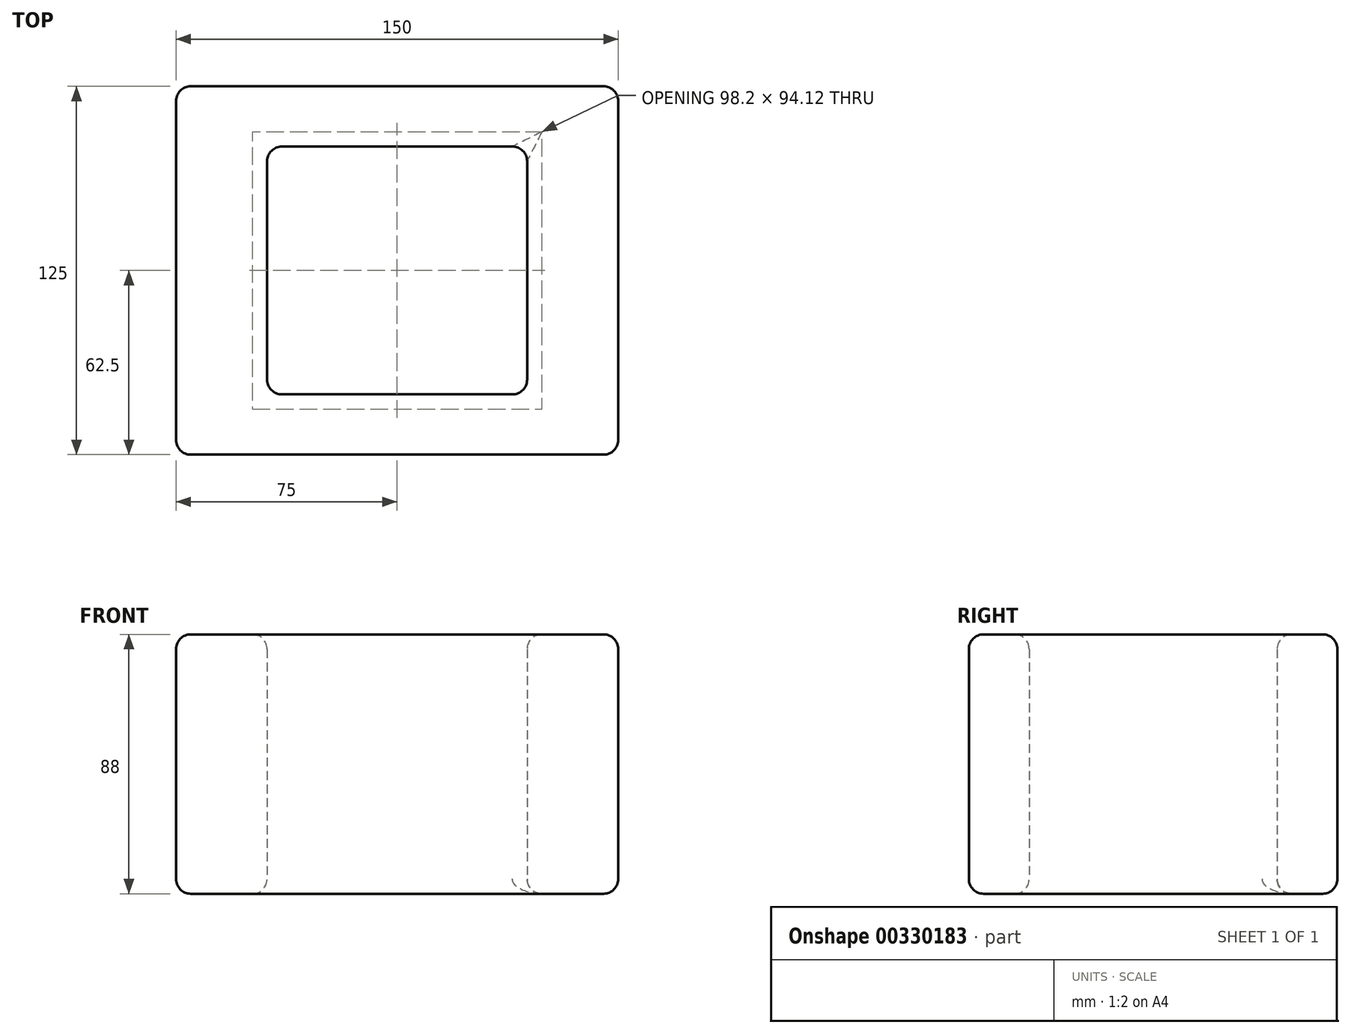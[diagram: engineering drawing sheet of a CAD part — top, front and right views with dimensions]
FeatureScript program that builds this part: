
annotation { "Feature Type Name" : "Feature", "Feature Type Description" : "" }
export const myFeature = defineFeature(function(context is Context, id is Id, definition is map)
    precondition{}
    {
        {
            var Q0;
            Q0=qCreatedBy(makeId("Top.planeOp"),FACE);
            var sketch = newSketch(context, id + "F0", { "sketchPlane" : qUnion([Q0])});
            skLineSegment(sketch, "E0.bottom", {"start": v(75, -62.5) * mm, "end": v(-75, -62.5) * mm});
            skLineSegment(sketch, "E0.top", {"start": v(75, 62.5) * mm, "end": v(-75, 62.5) * mm});
            skLineSegment(sketch, "E0.left", {"start": v(75, -62.5) * mm, "end": v(75, 62.5) * mm});
            skLineSegment(sketch, "E0.right", {"start": v(-75, -62.5) * mm, "end": v(-75, 62.5) * mm});
            skPoint(sketch, "E0.middle", {"position": v(0, 0) * mm});
            skLineSegment(sketch, "E1.bottom", {"start": v(-44.1, 42.06) * mm, "end": v(44.1, 42.06) * mm});
            skLineSegment(sketch, "E1.top", {"start": v(-44.1, -42.06) * mm, "end": v(44.1, -42.06) * mm});
            skLineSegment(sketch, "E1.left", {"start": v(-44.1, 42.06) * mm, "end": v(-44.1, -42.06) * mm});
            skLineSegment(sketch, "E1.right", {"start": v(44.1, 42.06) * mm, "end": v(44.1, -42.06) * mm});
            skSolve(sketch);
        }
        {
            var Q0;
            Q0 = qSketchRegion(id + "F0", true);
            extrude(context, id + "F1", {"entities" : qUnion([Q0]), "depth" : 88 * mm});
        }
        {
            var Q0;
            Q0=makeQuery(id+"F1.opExtrude","CAP_EDGE",EDGE,{"disambiguationData":[OSD([sQuery(id+"F0.wireOp",EDGE,"E0.right")])],"isStart":false});
            var Q1;
            Q1=makeQuery(id+"F1.opExtrude","SWEPT_FACE",FACE,{"disambiguationData":[OSD([sQuery(id+"F0.wireOp",EDGE,"E0.right")])]});
            fillet(context, id + "F2", {"entities" : qUnion([Q0, Q1]), "radius" : 5 * mm, "tangentPropagation" : true, "allowEdgeOverflow" : false});
        }
        {
            var Q0;
            Q0=makeQuery(id+"F1.opExtrude","SWEPT_FACE",FACE,{"disambiguationData":[OSD([sQuery(id+"F0.wireOp",EDGE,"E0.bottom")])]});
            fillet(context, id + "F3", {"entities" : qUnion([Q0]), "radius" : 5 * mm, "tangentPropagation" : true, "allowEdgeOverflow" : false});
        }
        {
            var Q0;
            Q0=makeQuery(id+"F1.opExtrude","SWEPT_FACE",FACE,{"disambiguationData":[OSD([sQuery(id+"F0.wireOp",EDGE,"E0.right")])]});
            var Q1;
            {var subQ0=sQuery(id+"F0.wireOp",EDGE,"E0.right");Q1=makeQuery(id+"F2.opFillet","BLEND_FACE",FACE,{"disambiguationData":[OSD([subQ0]),TDD([makeQuery(id+"F1.opExtrude","CAP_EDGE",EDGE,{"disambiguationData":[OSD([subQ0])],"isStart":true})])]});}
            var Q2;
            {var subQ0=sQuery(id+"F0.wireOp",EDGE,"E0.right");Q2=makeQuery(id+"F2.opFillet","BLEND_EDGE",EDGE,{"blendedFrom":[makeQuery(id+"F1.opExtrude","CAP_EDGE",EDGE,{"disambiguationData":[OSD([subQ0])],"isStart":true}),makeQuery(id+"F1.opExtrude","SWEPT_FACE",FACE,{"disambiguationData":[OSD([subQ0])]})],"blendedInto":[makeQuery(id+"F1.opExtrude","SWEPT_FACE",FACE,{"disambiguationData":[OSD([subQ0])]})]});}
            var Q3;
            Q3=makeQuery(id+"F2.opFillet","BLEND_FACE",FACE,{"disambiguationData":[OSD([sQuery(id+"F0.wireOp",EDGE,"E0.bottom"),sQuery(id+"F0.wireOp",EDGE,"E0.right")])]});
            var Q4;
            Q4=makeQuery(id+"F1.opExtrude","CAP_FACE",FACE,{"disambiguationData":[OSD([sQuery(id+"F0.wireOp",EDGE,"E0.bottom"),sQuery(id+"F0.wireOp",EDGE,"E0.top"),sQuery(id+"F0.wireOp",EDGE,"E0.left"),sQuery(id+"F0.wireOp",EDGE,"E0.right"),sQuery(id+"F0.wireOp",EDGE,"E1.bottom"),sQuery(id+"F0.wireOp",EDGE,"E1.top"),sQuery(id+"F0.wireOp",EDGE,"E1.left"),sQuery(id+"F0.wireOp",EDGE,"E1.right")])],"isStart":true});
            var Q5;
            Q5=makeQuery(id+"F1.opExtrude","SWEPT_FACE",FACE,{"disambiguationData":[OSD([sQuery(id+"F0.wireOp",EDGE,"E1.top")])]});
            var Q6;
            {var subQ0=sQuery(id+"F0.wireOp",EDGE,"E0.right");Q6=makeQuery(id+"F2.opFillet","BLEND_EDGE",EDGE,{"blendedFrom":[makeQuery(id+"F1.opExtrude","SWEPT_EDGE",EDGE,{"disambiguationData":[OSD([sQuery(id+"F0.wireOp",EDGE,"E0.bottom"),subQ0])]}),makeQuery(id+"F1.opExtrude","SWEPT_FACE",FACE,{"disambiguationData":[OSD([subQ0])]})],"blendedInto":[makeQuery(id+"F1.opExtrude","SWEPT_FACE",FACE,{"disambiguationData":[OSD([subQ0])]})]});}
            var Q7;
            Q7=makeQuery(id+"F1.opExtrude","SWEPT_FACE",FACE,{"disambiguationData":[OSD([sQuery(id+"F0.wireOp",EDGE,"E1.left")])]});
            var Q8;
            Q8=makeQuery(id+"F1.opExtrude","SWEPT_EDGE",EDGE,{"disambiguationData":[OSD([sQuery(id+"F0.wireOp",EDGE,"E1.top"),sQuery(id+"F0.wireOp",EDGE,"E1.left")])]});
            var Q9;
            {var subQ0=sQuery(id+"F0.wireOp",EDGE,"E0.right");Q9=makeQuery(id+"F2.opFillet","BLEND_EDGE",EDGE,{"blendedFrom":[makeQuery(id+"F1.opExtrude","CAP_EDGE",EDGE,{"disambiguationData":[OSD([subQ0])],"isStart":true}),makeQuery(id+"F1.opExtrude","CAP_FACE",FACE,{"disambiguationData":[OSD([sQuery(id+"F0.wireOp",EDGE,"E0.bottom"),sQuery(id+"F0.wireOp",EDGE,"E0.top"),sQuery(id+"F0.wireOp",EDGE,"E0.left"),subQ0,sQuery(id+"F0.wireOp",EDGE,"E1.bottom"),sQuery(id+"F0.wireOp",EDGE,"E1.top"),sQuery(id+"F0.wireOp",EDGE,"E1.left"),sQuery(id+"F0.wireOp",EDGE,"E1.right")])],"isStart":true})],"blendedInto":[makeQuery(id+"F1.opExtrude","CAP_FACE",FACE,{"disambiguationData":[OSD([sQuery(id+"F0.wireOp",EDGE,"E0.bottom"),sQuery(id+"F0.wireOp",EDGE,"E0.top"),sQuery(id+"F0.wireOp",EDGE,"E0.left"),subQ0,sQuery(id+"F0.wireOp",EDGE,"E1.bottom"),sQuery(id+"F0.wireOp",EDGE,"E1.top"),sQuery(id+"F0.wireOp",EDGE,"E1.left"),sQuery(id+"F0.wireOp",EDGE,"E1.right")])],"isStart":true})]});}
            var Q10;
            {var subQ0=sQuery(id+"F0.wireOp",EDGE,"E0.bottom");Q10=makeQuery(id+"F2.opFillet","BLEND_EDGE",EDGE,{"blendedFrom":[makeQuery(id+"F1.opExtrude","SWEPT_EDGE",EDGE,{"disambiguationData":[OSD([subQ0,sQuery(id+"F0.wireOp",EDGE,"E0.right")])]}),makeQuery(id+"F1.opExtrude","SWEPT_FACE",FACE,{"disambiguationData":[OSD([subQ0])]})],"blendedInto":[makeQuery(id+"F1.opExtrude","SWEPT_FACE",FACE,{"disambiguationData":[OSD([subQ0])]})]});}
            var Q11;
            Q11=makeQuery(id+"F1.opExtrude","CAP_EDGE",EDGE,{"disambiguationData":[OSD([sQuery(id+"F0.wireOp",EDGE,"E1.left")])],"isStart":true});
            var Q12;
            Q12=makeQuery(id+"F1.opExtrude","SWEPT_FACE",FACE,{"disambiguationData":[OSD([sQuery(id+"F0.wireOp",EDGE,"E0.bottom")])]});
            fillet(context, id + "F4", {"entities" : qUnion([Q0, Q1, Q2, Q3, Q4, Q5, Q6, Q7, Q8, Q9, Q10, Q11, Q12]), "radius" : 5 * mm, "tangentPropagation" : true, "allowEdgeOverflow" : false});
        }
        {
            var Q0;
            {var subQ0=sQuery(id+"F0.wireOp",EDGE,"E0.bottom");Q0=makeQuery(id+"F3.opFillet","BLEND_FACE",FACE,{"disambiguationData":[OSD([subQ0]),TDD([makeQuery(id+"F1.opExtrude","CAP_EDGE",EDGE,{"disambiguationData":[OSD([subQ0])],"isStart":true})])]});}
            var Q1;
            {var subQ0=sQuery(id+"F0.wireOp",EDGE,"E0.right");Q1=makeQuery(id+"F2.opFillet","BLEND_FACE",FACE,{"disambiguationData":[OSD([subQ0]),TDD([makeQuery(id+"F1.opExtrude","CAP_EDGE",EDGE,{"disambiguationData":[OSD([subQ0])],"isStart":true})])]});}
            var Q2;
            {var subQ0=sQuery(id+"F0.wireOp",EDGE,"E0.right");var subQ1=sQuery(id+"F0.wireOp",EDGE,"E0.bottom");Q2=makeQuery(id+"F4.opFillet","BLEND_FACE",FACE,{"disambiguationData":[OSD([subQ1,subQ0]),TDD([makeQuery(id+"F3.opFillet","BLEND_EDGE",EDGE,{"blendedFrom":[makeQuery(id+"F1.opExtrude","CAP_EDGE",EDGE,{"disambiguationData":[OSD([subQ1])],"isStart":true}),makeQuery(id+"F2.opFillet","BLEND_FACE",FACE,{"disambiguationData":[OSD([subQ0]),TDD([makeQuery(id+"F1.opExtrude","CAP_EDGE",EDGE,{"disambiguationData":[OSD([subQ0])],"isStart":true})])]})],"blendedInto":[makeQuery(id+"F2.opFillet","BLEND_FACE",FACE,{"disambiguationData":[OSD([subQ0]),TDD([makeQuery(id+"F1.opExtrude","CAP_EDGE",EDGE,{"disambiguationData":[OSD([subQ0])],"isStart":true})])]})]})])]});}
            var Q3;
            Q3=makeQuery(id+"F1.opExtrude","CAP_FACE",FACE,{"disambiguationData":[OSD([sQuery(id+"F0.wireOp",EDGE,"E0.bottom"),sQuery(id+"F0.wireOp",EDGE,"E0.top"),sQuery(id+"F0.wireOp",EDGE,"E0.left"),sQuery(id+"F0.wireOp",EDGE,"E0.right"),sQuery(id+"F0.wireOp",EDGE,"E1.bottom"),sQuery(id+"F0.wireOp",EDGE,"E1.top"),sQuery(id+"F0.wireOp",EDGE,"E1.left"),sQuery(id+"F0.wireOp",EDGE,"E1.right")])],"isStart":true});
            var Q4;
            Q4=makeQuery(id+"F1.opExtrude","SWEPT_FACE",FACE,{"disambiguationData":[OSD([sQuery(id+"F0.wireOp",EDGE,"E0.bottom")])]});
            var Q5;
            {var subQ0=sQuery(id+"F0.wireOp",EDGE,"E0.right");var subQ1=makeQuery(id+"F1.opExtrude","CAP_EDGE",EDGE,{"disambiguationData":[OSD([subQ0])],"isStart":true});Q5=makeQuery(id+"F4.opFillet","BLEND_EDGE",EDGE,{"blendedFrom":[makeQuery(id+"F2.opFillet","BLEND_EDGE",EDGE,{"blendedFrom":[makeQuery(id+"F1.opExtrude","SWEPT_EDGE",EDGE,{"disambiguationData":[OSD([sQuery(id+"F0.wireOp",EDGE,"E0.bottom"),subQ0])]}),subQ1],"blendedInto":[]}),makeQuery(id+"F2.opFillet","BLEND_FACE",FACE,{"disambiguationData":[OSD([subQ0]),TDD([subQ1])]})],"blendedInto":[makeQuery(id+"F2.opFillet","BLEND_FACE",FACE,{"disambiguationData":[OSD([subQ0]),TDD([subQ1])]})]});}
            var Q6;
            {var subQ0=sQuery(id+"F0.wireOp",EDGE,"E0.bottom");var subQ1=makeQuery(id+"F1.opExtrude","CAP_EDGE",EDGE,{"disambiguationData":[OSD([subQ0])],"isStart":true});var subQ2=sQuery(id+"F0.wireOp",EDGE,"E0.right");Q6=makeQuery(id+"F4.opFillet","BLEND_EDGE",EDGE,{"blendedFrom":[makeQuery(id+"F3.opFillet","BLEND_EDGE",EDGE,{"blendedFrom":[subQ1,makeQuery(id+"F2.opFillet","BLEND_FACE",FACE,{"disambiguationData":[OSD([subQ2]),TDD([makeQuery(id+"F1.opExtrude","CAP_EDGE",EDGE,{"disambiguationData":[OSD([subQ2])],"isStart":true})])]})],"blendedInto":[makeQuery(id+"F2.opFillet","BLEND_FACE",FACE,{"disambiguationData":[OSD([subQ2]),TDD([makeQuery(id+"F1.opExtrude","CAP_EDGE",EDGE,{"disambiguationData":[OSD([subQ2])],"isStart":true})])]})]}),makeQuery(id+"F3.opFillet","BLEND_FACE",FACE,{"disambiguationData":[OSD([subQ0]),TDD([subQ1])]})],"blendedInto":[makeQuery(id+"F3.opFillet","BLEND_FACE",FACE,{"disambiguationData":[OSD([subQ0]),TDD([subQ1])]})]});}
            var Q7;
            {var subQ0=sQuery(id+"F0.wireOp",EDGE,"E0.bottom");Q7=makeQuery(id+"F3.opFillet","BLEND_EDGE",EDGE,{"blendedFrom":[makeQuery(id+"F1.opExtrude","CAP_EDGE",EDGE,{"disambiguationData":[OSD([subQ0])],"isStart":true}),makeQuery(id+"F1.opExtrude","CAP_FACE",FACE,{"disambiguationData":[OSD([subQ0,sQuery(id+"F0.wireOp",EDGE,"E0.top"),sQuery(id+"F0.wireOp",EDGE,"E0.left"),sQuery(id+"F0.wireOp",EDGE,"E0.right"),sQuery(id+"F0.wireOp",EDGE,"E1.bottom"),sQuery(id+"F0.wireOp",EDGE,"E1.top"),sQuery(id+"F0.wireOp",EDGE,"E1.left"),sQuery(id+"F0.wireOp",EDGE,"E1.right")])],"isStart":true})],"blendedInto":[makeQuery(id+"F1.opExtrude","CAP_FACE",FACE,{"disambiguationData":[OSD([subQ0,sQuery(id+"F0.wireOp",EDGE,"E0.top"),sQuery(id+"F0.wireOp",EDGE,"E0.left"),sQuery(id+"F0.wireOp",EDGE,"E0.right"),sQuery(id+"F0.wireOp",EDGE,"E1.bottom"),sQuery(id+"F0.wireOp",EDGE,"E1.top"),sQuery(id+"F0.wireOp",EDGE,"E1.left"),sQuery(id+"F0.wireOp",EDGE,"E1.right")])],"isStart":true})]});}
            var Q8;
            {var subQ0=sQuery(id+"F0.wireOp",EDGE,"E0.bottom");Q8=makeQuery(id+"F3.opFillet","BLEND_EDGE",EDGE,{"blendedFrom":[makeQuery(id+"F1.opExtrude","CAP_EDGE",EDGE,{"disambiguationData":[OSD([subQ0])],"isStart":true}),makeQuery(id+"F1.opExtrude","SWEPT_FACE",FACE,{"disambiguationData":[OSD([subQ0])]})],"blendedInto":[makeQuery(id+"F1.opExtrude","SWEPT_FACE",FACE,{"disambiguationData":[OSD([subQ0])]})]});}
            var Q9;
            {var subQ0=sQuery(id+"F0.wireOp",EDGE,"E1.left");var subQ1=sQuery(id+"F0.wireOp",EDGE,"E1.top");Q9=makeQuery(id+"F4.opFillet","BLEND_FACE",FACE,{"disambiguationData":[OSD([subQ1,subQ0]),TDD([makeQuery(id+"F1.opExtrude","SWEPT_EDGE",EDGE,{"disambiguationData":[OSD([subQ1,subQ0])]})])]});}
            var Q10;
            Q10=makeQuery(id+"F1.opExtrude","SWEPT_FACE",FACE,{"disambiguationData":[OSD([sQuery(id+"F0.wireOp",EDGE,"E0.right")])]});
            var Q11;
            {var subQ0=sQuery(id+"F0.wireOp",EDGE,"E0.right");Q11=makeQuery(id+"F2.opFillet","BLEND_EDGE",EDGE,{"blendedFrom":[makeQuery(id+"F1.opExtrude","CAP_EDGE",EDGE,{"disambiguationData":[OSD([subQ0])],"isStart":true}),makeQuery(id+"F1.opExtrude","SWEPT_FACE",FACE,{"disambiguationData":[OSD([subQ0])]})],"blendedInto":[makeQuery(id+"F1.opExtrude","SWEPT_FACE",FACE,{"disambiguationData":[OSD([subQ0])]})]});}
            var Q12;
            Q12=makeQuery(id+"F2.opFillet","BLEND_FACE",FACE,{"disambiguationData":[OSD([sQuery(id+"F0.wireOp",EDGE,"E0.bottom"),sQuery(id+"F0.wireOp",EDGE,"E0.right")])]});
            var Q13;
            {var subQ0=sQuery(id+"F0.wireOp",EDGE,"E0.right");Q13=makeQuery(id+"F2.opFillet","BLEND_EDGE",EDGE,{"blendedFrom":[makeQuery(id+"F1.opExtrude","CAP_EDGE",EDGE,{"disambiguationData":[OSD([subQ0])],"isStart":true}),makeQuery(id+"F1.opExtrude","CAP_FACE",FACE,{"disambiguationData":[OSD([sQuery(id+"F0.wireOp",EDGE,"E0.bottom"),sQuery(id+"F0.wireOp",EDGE,"E0.top"),sQuery(id+"F0.wireOp",EDGE,"E0.left"),subQ0,sQuery(id+"F0.wireOp",EDGE,"E1.bottom"),sQuery(id+"F0.wireOp",EDGE,"E1.top"),sQuery(id+"F0.wireOp",EDGE,"E1.left"),sQuery(id+"F0.wireOp",EDGE,"E1.right")])],"isStart":true})],"blendedInto":[makeQuery(id+"F1.opExtrude","CAP_FACE",FACE,{"disambiguationData":[OSD([sQuery(id+"F0.wireOp",EDGE,"E0.bottom"),sQuery(id+"F0.wireOp",EDGE,"E0.top"),sQuery(id+"F0.wireOp",EDGE,"E0.left"),subQ0,sQuery(id+"F0.wireOp",EDGE,"E1.bottom"),sQuery(id+"F0.wireOp",EDGE,"E1.top"),sQuery(id+"F0.wireOp",EDGE,"E1.left"),sQuery(id+"F0.wireOp",EDGE,"E1.right")])],"isStart":true})]});}
            var Q14;
            Q14=makeQuery(id+"F1.opExtrude","SWEPT_FACE",FACE,{"disambiguationData":[OSD([sQuery(id+"F0.wireOp",EDGE,"E1.top")])]});
            var Q15;
            Q15=makeQuery(id+"F1.opExtrude","SWEPT_FACE",FACE,{"disambiguationData":[OSD([sQuery(id+"F0.wireOp",EDGE,"E1.left")])]});
            var Q16;
            {var subQ0=sQuery(id+"F0.wireOp",EDGE,"E1.right");var subQ1=sQuery(id+"F0.wireOp",EDGE,"E1.top");Q16=makeQuery(id+"F4.opFillet","BLEND_FACE",FACE,{"disambiguationData":[OSD([subQ1,subQ0]),TDD([makeQuery(id+"F1.opExtrude","CAP_VERTEX",VERTEX,{"disambiguationData":[OSD([subQ1,subQ0])],"isStart":false})])]});}
            var Q17;
            Q17=makeQuery(id+"F1.opExtrude","CAP_EDGE",EDGE,{"disambiguationData":[OSD([sQuery(id+"F0.wireOp",EDGE,"E0.left")])],"isStart":false});
            var Q18;
            {var subQ0=sQuery(id+"F0.wireOp",EDGE,"E1.bottom");Q18=makeQuery(id+"F4.opFillet","BLEND_FACE",FACE,{"disambiguationData":[OSD([subQ0]),TDD([makeQuery(id+"F1.opExtrude","CAP_EDGE",EDGE,{"disambiguationData":[OSD([subQ0])],"isStart":false})])]});}
            var Q19;
            {var subQ0=sQuery(id+"F0.wireOp",EDGE,"E1.top");Q19=makeQuery(id+"F4.opFillet","BLEND_FACE",FACE,{"disambiguationData":[OSD([subQ0]),TDD([makeQuery(id+"F1.opExtrude","CAP_EDGE",EDGE,{"disambiguationData":[OSD([subQ0])],"isStart":false})])]});}
            var Q20;
            {var subQ0=sQuery(id+"F0.wireOp",EDGE,"E1.right");var subQ1=sQuery(id+"F0.wireOp",EDGE,"E1.top");Q20=makeQuery(id+"F4.opFillet","BLEND_FACE",FACE,{"disambiguationData":[OSD([subQ1,subQ0]),TDD([makeQuery(id+"F1.opExtrude","SWEPT_EDGE",EDGE,{"disambiguationData":[OSD([subQ1,subQ0])]})])]});}
            var Q21;
            {var subQ0=sQuery(id+"F0.wireOp",EDGE,"E0.right");Q21=makeQuery(id+"F2.opFillet","BLEND_EDGE",EDGE,{"blendedFrom":[makeQuery(id+"F1.opExtrude","SWEPT_EDGE",EDGE,{"disambiguationData":[OSD([sQuery(id+"F0.wireOp",EDGE,"E0.bottom"),subQ0])]}),makeQuery(id+"F1.opExtrude","SWEPT_FACE",FACE,{"disambiguationData":[OSD([subQ0])]})],"blendedInto":[makeQuery(id+"F1.opExtrude","SWEPT_FACE",FACE,{"disambiguationData":[OSD([subQ0])]})]});}
            var Q22;
            {var subQ0=sQuery(id+"F0.wireOp",EDGE,"E0.bottom");Q22=makeQuery(id+"F2.opFillet","BLEND_EDGE",EDGE,{"blendedFrom":[makeQuery(id+"F1.opExtrude","SWEPT_EDGE",EDGE,{"disambiguationData":[OSD([subQ0,sQuery(id+"F0.wireOp",EDGE,"E0.right")])]}),makeQuery(id+"F1.opExtrude","SWEPT_FACE",FACE,{"disambiguationData":[OSD([subQ0])]})],"blendedInto":[makeQuery(id+"F1.opExtrude","SWEPT_FACE",FACE,{"disambiguationData":[OSD([subQ0])]})]});}
            var Q23;
            {var subQ0=sQuery(id+"F0.wireOp",EDGE,"E1.right");Q23=makeQuery(id+"F4.opFillet","BLEND_EDGE",EDGE,{"blendedFrom":[makeQuery(id+"F1.opExtrude","CAP_EDGE",EDGE,{"disambiguationData":[OSD([subQ0])],"isStart":false}),makeQuery(id+"F1.opExtrude","SWEPT_FACE",FACE,{"disambiguationData":[OSD([subQ0])]})],"blendedInto":[makeQuery(id+"F1.opExtrude","SWEPT_FACE",FACE,{"disambiguationData":[OSD([subQ0])]})]});}
            var Q24;
            {var subQ0=sQuery(id+"F0.wireOp",EDGE,"E1.right");Q24=makeQuery(id+"F4.opFillet","BLEND_FACE",FACE,{"disambiguationData":[OSD([subQ0]),TDD([makeQuery(id+"F1.opExtrude","CAP_EDGE",EDGE,{"disambiguationData":[OSD([subQ0])],"isStart":false})])]});}
            var Q25;
            Q25=makeQuery(id+"F1.opExtrude","SWEPT_FACE",FACE,{"disambiguationData":[OSD([sQuery(id+"F0.wireOp",EDGE,"E0.left")])]});
            var Q26;
            {var subQ0=sQuery(id+"F0.wireOp",EDGE,"E1.bottom");Q26=makeQuery(id+"F4.opFillet","BLEND_EDGE",EDGE,{"blendedFrom":[makeQuery(id+"F1.opExtrude","CAP_EDGE",EDGE,{"disambiguationData":[OSD([subQ0])],"isStart":false}),makeQuery(id+"F1.opExtrude","SWEPT_FACE",FACE,{"disambiguationData":[OSD([subQ0])]})],"blendedInto":[makeQuery(id+"F1.opExtrude","SWEPT_FACE",FACE,{"disambiguationData":[OSD([subQ0])]})]});}
            var Q27;
            Q27=makeQuery(id+"F1.opExtrude","CAP_FACE",FACE,{"disambiguationData":[OSD([sQuery(id+"F0.wireOp",EDGE,"E0.bottom"),sQuery(id+"F0.wireOp",EDGE,"E0.top"),sQuery(id+"F0.wireOp",EDGE,"E0.left"),sQuery(id+"F0.wireOp",EDGE,"E0.right"),sQuery(id+"F0.wireOp",EDGE,"E1.bottom"),sQuery(id+"F0.wireOp",EDGE,"E1.top"),sQuery(id+"F0.wireOp",EDGE,"E1.left"),sQuery(id+"F0.wireOp",EDGE,"E1.right")])],"isStart":false});
            var Q28;
            {var subQ0=sQuery(id+"F0.wireOp",EDGE,"E1.top");Q28=makeQuery(id+"F4.opFillet","BLEND_EDGE",EDGE,{"blendedFrom":[makeQuery(id+"F1.opExtrude","CAP_EDGE",EDGE,{"disambiguationData":[OSD([subQ0])],"isStart":false}),makeQuery(id+"F1.opExtrude","SWEPT_FACE",FACE,{"disambiguationData":[OSD([subQ0])]})],"blendedInto":[makeQuery(id+"F1.opExtrude","SWEPT_FACE",FACE,{"disambiguationData":[OSD([subQ0])]})]});}
            var Q29;
            Q29=makeQuery(id+"F1.opExtrude","SWEPT_FACE",FACE,{"disambiguationData":[OSD([sQuery(id+"F0.wireOp",EDGE,"E1.bottom")])]});
            var Q30;
            Q30=makeQuery(id+"F1.opExtrude","SWEPT_FACE",FACE,{"disambiguationData":[OSD([sQuery(id+"F0.wireOp",EDGE,"E1.right")])]});
            var Q31;
            {var subQ0=sQuery(id+"F0.wireOp",EDGE,"E1.top");Q31=makeQuery(id+"F4.opFillet","BLEND_EDGE",EDGE,{"blendedFrom":[makeQuery(id+"F1.opExtrude","SWEPT_EDGE",EDGE,{"disambiguationData":[OSD([subQ0,sQuery(id+"F0.wireOp",EDGE,"E1.left")])]}),makeQuery(id+"F1.opExtrude","SWEPT_FACE",FACE,{"disambiguationData":[OSD([subQ0])]})],"blendedInto":[makeQuery(id+"F1.opExtrude","SWEPT_FACE",FACE,{"disambiguationData":[OSD([subQ0])]})]});}
            var Q32;
            {var subQ0=sQuery(id+"F0.wireOp",EDGE,"E1.left");Q32=makeQuery(id+"F4.opFillet","BLEND_EDGE",EDGE,{"blendedFrom":[makeQuery(id+"F1.opExtrude","SWEPT_EDGE",EDGE,{"disambiguationData":[OSD([sQuery(id+"F0.wireOp",EDGE,"E1.top"),subQ0])]}),makeQuery(id+"F1.opExtrude","SWEPT_FACE",FACE,{"disambiguationData":[OSD([subQ0])]})],"blendedInto":[makeQuery(id+"F1.opExtrude","SWEPT_FACE",FACE,{"disambiguationData":[OSD([subQ0])]})]});}
            var Q33;
            {var subQ0=sQuery(id+"F0.wireOp",EDGE,"E0.right");var subQ1=sQuery(id+"F0.wireOp",EDGE,"E0.bottom");Q33=makeQuery(id+"F4.opFillet","BLEND_EDGE",EDGE,{"blendedFrom":[makeQuery(id+"F2.opFillet","BLEND_EDGE",EDGE,{"blendedFrom":[makeQuery(id+"F1.opExtrude","SWEPT_EDGE",EDGE,{"disambiguationData":[OSD([subQ1,subQ0])]}),makeQuery(id+"F1.opExtrude","CAP_EDGE",EDGE,{"disambiguationData":[OSD([subQ0])],"isStart":true})],"blendedInto":[]}),makeQuery(id+"F2.opFillet","BLEND_FACE",FACE,{"disambiguationData":[OSD([subQ1,subQ0])]})],"blendedInto":[makeQuery(id+"F2.opFillet","BLEND_FACE",FACE,{"disambiguationData":[OSD([subQ1,subQ0])]})]});}
            var Q34;
            {var subQ0=sQuery(id+"F0.wireOp",EDGE,"E1.top");Q34=makeQuery(id+"F4.opFillet","BLEND_EDGE",EDGE,{"blendedFrom":[makeQuery(id+"F1.opExtrude","SWEPT_EDGE",EDGE,{"disambiguationData":[OSD([subQ0,sQuery(id+"F0.wireOp",EDGE,"E1.right")])]}),makeQuery(id+"F1.opExtrude","SWEPT_FACE",FACE,{"disambiguationData":[OSD([subQ0])]})],"blendedInto":[makeQuery(id+"F1.opExtrude","SWEPT_FACE",FACE,{"disambiguationData":[OSD([subQ0])]})]});}
            var Q35;
            {var subQ0=sQuery(id+"F0.wireOp",EDGE,"E1.right");Q35=makeQuery(id+"F4.opFillet","BLEND_EDGE",EDGE,{"blendedFrom":[makeQuery(id+"F1.opExtrude","SWEPT_EDGE",EDGE,{"disambiguationData":[OSD([sQuery(id+"F0.wireOp",EDGE,"E1.top"),subQ0])]}),makeQuery(id+"F1.opExtrude","SWEPT_FACE",FACE,{"disambiguationData":[OSD([subQ0])]})],"blendedInto":[makeQuery(id+"F1.opExtrude","SWEPT_FACE",FACE,{"disambiguationData":[OSD([subQ0])]})]});}
            var Q36;
            {var subQ0=sQuery(id+"F0.wireOp",EDGE,"E1.right");Q36=makeQuery(id+"F4.opFillet","BLEND_EDGE",EDGE,{"blendedFrom":[makeQuery(id+"F1.opExtrude","CAP_EDGE",EDGE,{"disambiguationData":[OSD([subQ0])],"isStart":false}),makeQuery(id+"F1.opExtrude","CAP_FACE",FACE,{"disambiguationData":[OSD([sQuery(id+"F0.wireOp",EDGE,"E0.bottom"),sQuery(id+"F0.wireOp",EDGE,"E0.top"),sQuery(id+"F0.wireOp",EDGE,"E0.left"),sQuery(id+"F0.wireOp",EDGE,"E0.right"),sQuery(id+"F0.wireOp",EDGE,"E1.bottom"),sQuery(id+"F0.wireOp",EDGE,"E1.top"),sQuery(id+"F0.wireOp",EDGE,"E1.left"),subQ0])],"isStart":false})],"blendedInto":[makeQuery(id+"F1.opExtrude","CAP_FACE",FACE,{"disambiguationData":[OSD([sQuery(id+"F0.wireOp",EDGE,"E0.bottom"),sQuery(id+"F0.wireOp",EDGE,"E0.top"),sQuery(id+"F0.wireOp",EDGE,"E0.left"),sQuery(id+"F0.wireOp",EDGE,"E0.right"),sQuery(id+"F0.wireOp",EDGE,"E1.bottom"),sQuery(id+"F0.wireOp",EDGE,"E1.top"),sQuery(id+"F0.wireOp",EDGE,"E1.left"),subQ0])],"isStart":false})]});}
            var Q37;
            Q37=makeQuery(id+"F4.opFillet","BLEND_EDGE",EDGE,{"blendedFrom":[makeQuery(id+"F1.opExtrude","CAP_EDGE",EDGE,{"disambiguationData":[OSD([sQuery(id+"F0.wireOp",EDGE,"E1.bottom")])],"isStart":false}),makeQuery(id+"F1.opExtrude","CAP_EDGE",EDGE,{"disambiguationData":[OSD([sQuery(id+"F0.wireOp",EDGE,"E1.right")])],"isStart":false})],"blendedInto":[]});
            var Q38;
            {var subQ0=sQuery(id+"F0.wireOp",EDGE,"E1.right");var subQ1=sQuery(id+"F0.wireOp",EDGE,"E1.top");Q38=makeQuery(id+"F4.opFillet","BLEND_EDGE",EDGE,{"blendedFrom":[makeQuery(id+"F1.opExtrude","CAP_VERTEX",VERTEX,{"disambiguationData":[OSD([subQ1,subQ0])],"isStart":false}),makeQuery(id+"F1.opExtrude","SWEPT_EDGE",EDGE,{"disambiguationData":[OSD([subQ1,subQ0])]})],"blendedInto":[]});}
            var Q39;
            {var subQ0=sQuery(id+"F0.wireOp",EDGE,"E1.bottom");Q39=makeQuery(id+"F4.opFillet","BLEND_EDGE",EDGE,{"blendedFrom":[makeQuery(id+"F1.opExtrude","CAP_EDGE",EDGE,{"disambiguationData":[OSD([subQ0])],"isStart":false}),makeQuery(id+"F1.opExtrude","CAP_FACE",FACE,{"disambiguationData":[OSD([sQuery(id+"F0.wireOp",EDGE,"E0.bottom"),sQuery(id+"F0.wireOp",EDGE,"E0.top"),sQuery(id+"F0.wireOp",EDGE,"E0.left"),sQuery(id+"F0.wireOp",EDGE,"E0.right"),subQ0,sQuery(id+"F0.wireOp",EDGE,"E1.top"),sQuery(id+"F0.wireOp",EDGE,"E1.left"),sQuery(id+"F0.wireOp",EDGE,"E1.right")])],"isStart":false})],"blendedInto":[makeQuery(id+"F1.opExtrude","CAP_FACE",FACE,{"disambiguationData":[OSD([sQuery(id+"F0.wireOp",EDGE,"E0.bottom"),sQuery(id+"F0.wireOp",EDGE,"E0.top"),sQuery(id+"F0.wireOp",EDGE,"E0.left"),sQuery(id+"F0.wireOp",EDGE,"E0.right"),subQ0,sQuery(id+"F0.wireOp",EDGE,"E1.top"),sQuery(id+"F0.wireOp",EDGE,"E1.left"),sQuery(id+"F0.wireOp",EDGE,"E1.right")])],"isStart":false})]});}
            var Q40;
            {var subQ0=sQuery(id+"F0.wireOp",EDGE,"E1.top");Q40=makeQuery(id+"F4.opFillet","BLEND_EDGE",EDGE,{"blendedFrom":[makeQuery(id+"F1.opExtrude","CAP_VERTEX",VERTEX,{"disambiguationData":[OSD([subQ0,sQuery(id+"F0.wireOp",EDGE,"E1.right")])],"isStart":false}),makeQuery(id+"F1.opExtrude","CAP_EDGE",EDGE,{"disambiguationData":[OSD([subQ0])],"isStart":false})],"blendedInto":[]});}
            var Q41;
            {var subQ0=sQuery(id+"F0.wireOp",EDGE,"E1.right");Q41=makeQuery(id+"F4.opFillet","BLEND_EDGE",EDGE,{"blendedFrom":[makeQuery(id+"F1.opExtrude","CAP_VERTEX",VERTEX,{"disambiguationData":[OSD([sQuery(id+"F0.wireOp",EDGE,"E1.top"),subQ0])],"isStart":false}),makeQuery(id+"F1.opExtrude","CAP_EDGE",EDGE,{"disambiguationData":[OSD([subQ0])],"isStart":false})],"blendedInto":[]});}
            var Q42;
            {var subQ0=sQuery(id+"F0.wireOp",EDGE,"E1.right");var subQ1=sQuery(id+"F0.wireOp",EDGE,"E1.top");Q42=makeQuery(id+"F4.opFillet","BLEND_EDGE",EDGE,{"blendedFrom":[makeQuery(id+"F1.opExtrude","CAP_VERTEX",VERTEX,{"disambiguationData":[OSD([subQ1,subQ0])],"isStart":false}),makeQuery(id+"F1.opExtrude","CAP_FACE",FACE,{"disambiguationData":[OSD([sQuery(id+"F0.wireOp",EDGE,"E0.bottom"),sQuery(id+"F0.wireOp",EDGE,"E0.top"),sQuery(id+"F0.wireOp",EDGE,"E0.left"),sQuery(id+"F0.wireOp",EDGE,"E0.right"),sQuery(id+"F0.wireOp",EDGE,"E1.bottom"),subQ1,sQuery(id+"F0.wireOp",EDGE,"E1.left"),subQ0])],"isStart":false})],"blendedInto":[makeQuery(id+"F1.opExtrude","CAP_FACE",FACE,{"disambiguationData":[OSD([sQuery(id+"F0.wireOp",EDGE,"E0.bottom"),sQuery(id+"F0.wireOp",EDGE,"E0.top"),sQuery(id+"F0.wireOp",EDGE,"E0.left"),sQuery(id+"F0.wireOp",EDGE,"E0.right"),sQuery(id+"F0.wireOp",EDGE,"E1.bottom"),subQ1,sQuery(id+"F0.wireOp",EDGE,"E1.left"),subQ0])],"isStart":false})]});}
            fillet(context, id + "F5", {"entities" : qUnion([Q0, Q1, Q2, Q3, Q4, Q5, Q6, Q7, Q8, Q9, Q10, Q11, Q12, Q13, Q14, Q15, Q16, Q17, Q18, Q19, Q20, Q21, Q22, Q23, Q24, Q25, Q26, Q27, Q28, Q29, Q30, Q31, Q32, Q33, Q34, Q35, Q36, Q37, Q38, Q39, Q40, Q41, Q42]), "radius" : 5 * mm, "tangentPropagation" : true, "allowEdgeOverflow" : false});
        }
    });
